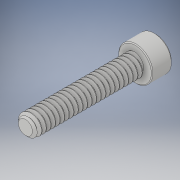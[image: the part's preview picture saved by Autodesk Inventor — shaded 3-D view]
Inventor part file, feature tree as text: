
AUTODESK INVENTOR PART (.ipt)
format: ipt  version: 2018 (Build 220112000, 112)  size: 894,464 bytes
history: native  units: in
note: dims shown in document units (in); Inventor stores cm internally (conversion verified against a paired STEP export)
features: chamfer x1
ambient origin geometry x8: Origin, YZ Plane, XZ Plane, XY Plane, X Axis, Y Axis, Z Axis, Center Point
bodies: Solid1 (feature_tree)
feature tree (1):
  chamfer  "Chamfer2"  [1 undecoded]
note: 1 required parameter value undecoded (feature->parameter linkage not recoverable at this tier; creation-order binding heuristic only, values carry confidence <= 0.55)
